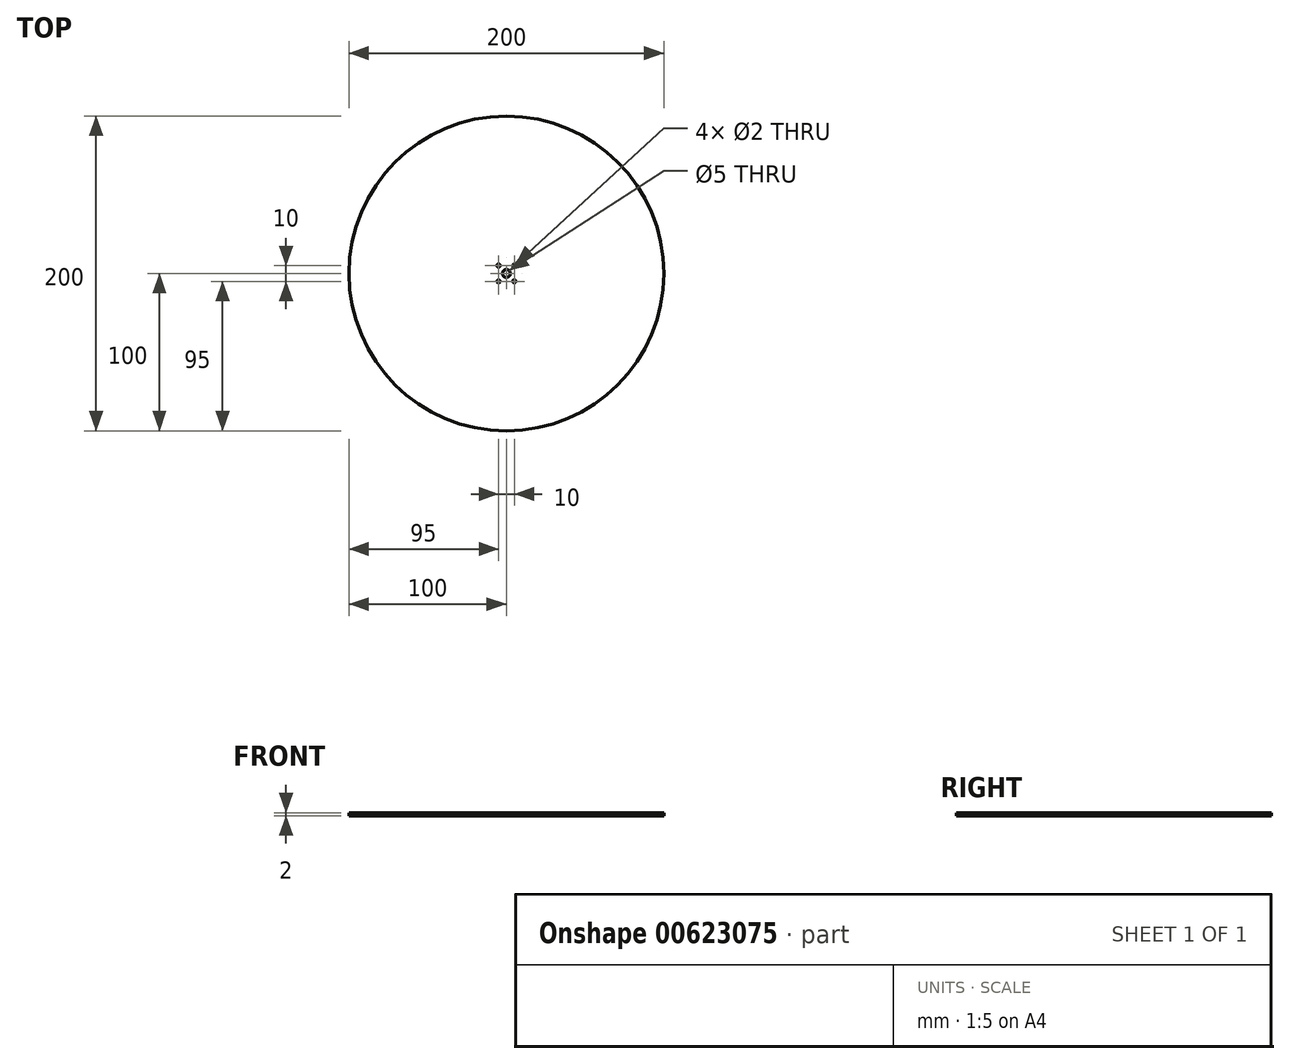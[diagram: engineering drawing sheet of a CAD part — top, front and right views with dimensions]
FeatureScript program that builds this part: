
annotation { "Feature Type Name" : "Feature", "Feature Type Description" : "" }
export const myFeature = defineFeature(function(context is Context, id is Id, definition is map)
    precondition{}
    {
        {
            var Q0;
            Q0=qCreatedBy(makeId("Top.planeOp"),FACE);
            var sketch = newSketch(context, id + "F0", { "sketchPlane" : qUnion([Q0])});
            skCircle(sketch, "E0", {"center": v(0, 0) * mm, "radius": 100 * mm});
            skCircle(sketch, "E1", {"center": v(0, 0) * mm, "radius": 2.5 * mm});
            skCircle(sketch, "E2", {"center": v(-5, 5) * mm, "radius": 1 * mm});
            skCircle(sketch, "E3", {"center": v(5, 5) * mm, "radius": 1 * mm});
            skCircle(sketch, "E4", {"center": v(-5, -5) * mm, "radius": 1 * mm});
            skCircle(sketch, "E5", {"center": v(5, -5) * mm, "radius": 1 * mm});
            skSolve(sketch);
        }
        {
            var Q0;
            Q0=makeQuery(id+"F0.imprint","IMPRINT",FACE,{"disambiguationData":[TD([[makeQuery(id+"F0.imprint","IMPRINT",EDGE,{"derivedFrom":sQuery(id+"F0.wireOp",EDGE,"E0")}),1.0]])]});
            extrude(context, id + "F1", {"entities" : qUnion([Q0]), "depth" : 2 * mm, "offsetDistance" : 25 * mm});
        }
    });
